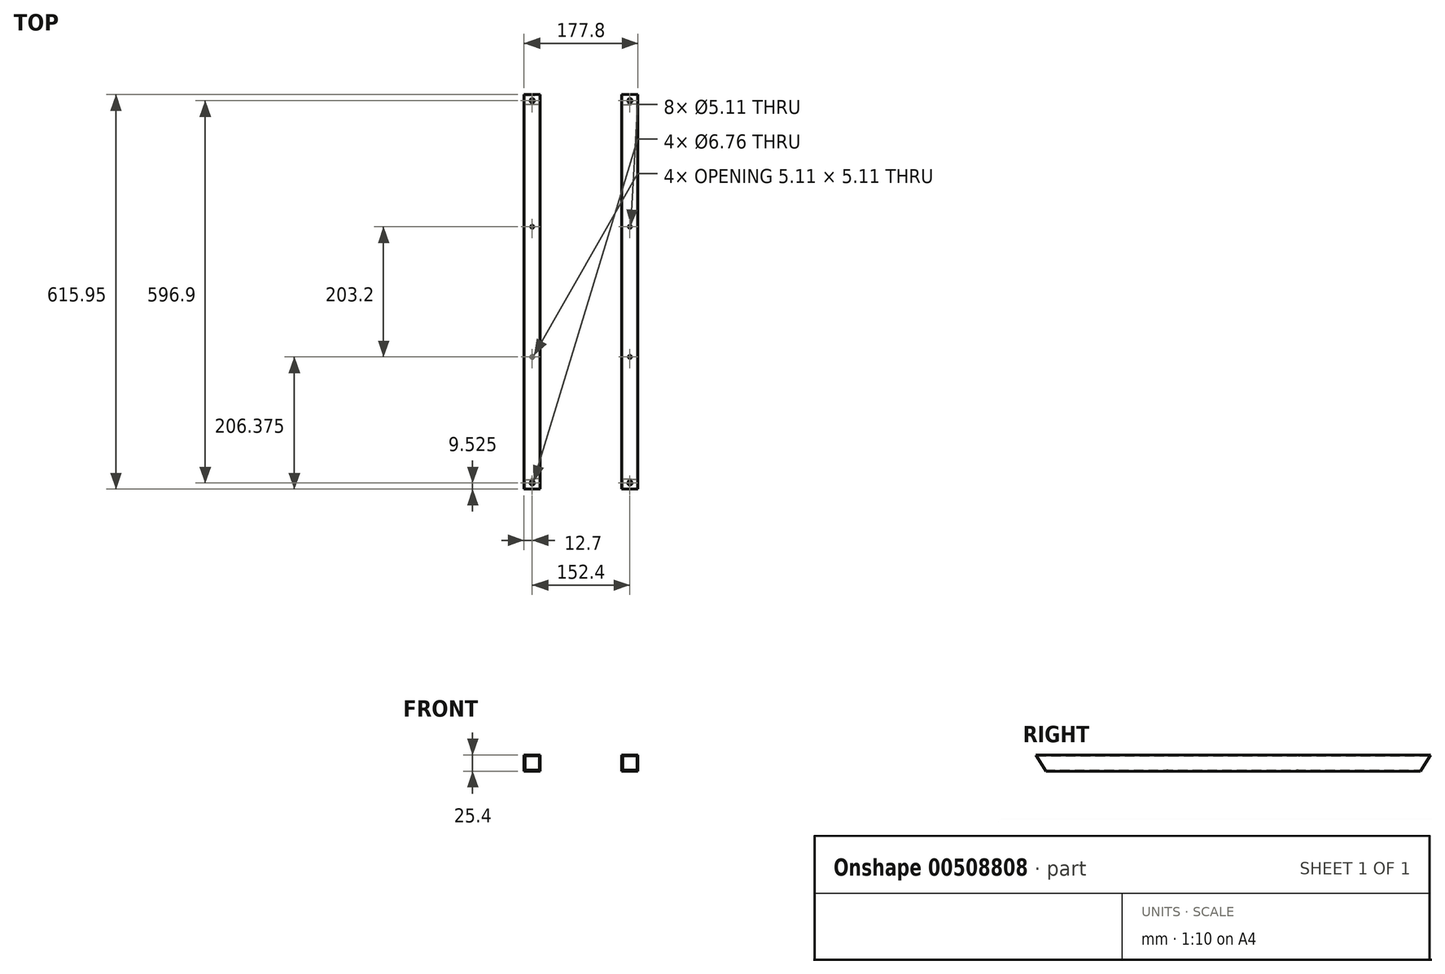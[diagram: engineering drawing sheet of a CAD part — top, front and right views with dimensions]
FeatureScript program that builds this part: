
annotation { "Feature Type Name" : "Feature", "Feature Type Description" : "" }
export const myFeature = defineFeature(function(context is Context, id is Id, definition is map)
    precondition{}
    {
        {
            var Q0;
            Q0=qCreatedBy(makeId("Front.planeOp"),FACE);
            var sketch = newSketch(context, id + "F0", { "sketchPlane" : qUnion([Q0])});
            skLineSegment(sketch, "E0.bottom", {"start": v(63.5, 25.4) * mm, "end": v(88.9, 25.4) * mm});
            skLineSegment(sketch, "E0.top", {"start": v(63.5, 0) * mm, "end": v(88.9, 0) * mm});
            skLineSegment(sketch, "E0.left", {"start": v(63.5, 25.4) * mm, "end": v(63.5, 0) * mm});
            skLineSegment(sketch, "E0.right", {"start": v(88.9, 25.4) * mm, "end": v(88.9, 0) * mm});
            skLineSegment(sketch, "E1.bottom", {"start": v(87.31, 1.59) * mm, "end": v(65.09, 1.59) * mm});
            skLineSegment(sketch, "E1.top", {"start": v(87.31, 23.81) * mm, "end": v(65.09, 23.81) * mm});
            skLineSegment(sketch, "E1.left", {"start": v(87.31, 1.59) * mm, "end": v(87.31, 23.81) * mm});
            skLineSegment(sketch, "E1.right", {"start": v(65.09, 1.59) * mm, "end": v(65.09, 23.81) * mm});
            skSolve(sketch);
        }
        {
            var Q0;
            Q0 = qSketchRegion(id + "F0", true);
            extrude(context, id + "F1", {"entities" : qUnion([Q0]), "depth" : 615.95 * mm, "offsetDistance" : 25.4 * mm});
        }
        {
            var Q0;
            Q0=makeQuery(id+"F1.opExtrude","SWEPT_FACE",FACE,{"disambiguationData":[OSD([sQuery(id+"F0.wireOp",EDGE,"E0.bottom")])]});
            var sketch = newSketch(context, id + "F2", { "sketchPlane" : qUnion([Q0])});
            skLineSegment(sketch, "E2", {"start": v(63.5, -307.98) * mm, "end": v(88.9, -307.98) * mm, "construction": true});
            skPoint(sketch, "E3", {"position": v(76.2, -409.58) * mm});
            skPoint(sketch, "E4.MirrorP", {"position": v(76.2, -206.38) * mm});
            skSolve(sketch);
        }
        {
            var Q0;
            Q0=sQuery(id+"F2.wireOp",VERTEX,"E4.MirrorP");
            var Q1;
            Q1=sQuery(id+"F2.wireOp",VERTEX,"E3");
            var Q2;
            Q2=makeQuery(id+"F1.opExtrude","SWEPT_BODY",BODY,{"disambiguationData":[OSD([sQuery(id+"F0.wireOp",EDGE,"E0.bottom"),sQuery(id+"F0.wireOp",EDGE,"E0.top"),sQuery(id+"F0.wireOp",EDGE,"E0.left"),sQuery(id+"F0.wireOp",EDGE,"E0.right"),sQuery(id+"F0.wireOp",EDGE,"E1.bottom"),sQuery(id+"F0.wireOp",EDGE,"E1.top"),sQuery(id+"F0.wireOp",EDGE,"E1.left"),sQuery(id+"F0.wireOp",EDGE,"E1.right")])]});
            hole(context, id + "F3", {"style" : HoleStyle.SIMPLE, "endStyle" : HoleEndStyle.THROUGH, "standardTappedOrClearance" : lookupTablePath({ "standard" : "ANSI", "fit" : "Normal (ASME)", "size" : "#10", "type" : "Clearance" }), "standardBlindInLast" : lookupTablePath({ "fit" : "Free", "standard" : "ANSI", "size" : "#10", "type" : "Clearance" }), "holeDiameter" : 5.1 * mm, "isTappedThrough" : true, "tappedDepth" : 12.7 * mm, "tapClearance" : 3, "locations" : qUnion([Q0, Q1]), "scope" : qUnion([Q2])});
        }
        {
            var Q0;
            Q0=makeQuery(id+"F1.opExtrude","SWEPT_FACE",FACE,{"disambiguationData":[OSD([sQuery(id+"F0.wireOp",EDGE,"E0.right")])]});
            var sketch = newSketch(context, id + "F4", { "sketchPlane" : qUnion([Q0])});
            skLineSegment(sketch, "E5", {"start": v(0, 25.4) * mm, "end": v(-15.88, 0) * mm});
            skLineSegment(sketch, "E6", {"start": v(-15.88, 0) * mm, "end": v(0, 0) * mm});
            skLineSegment(sketch, "E7", {"start": v(0, 0) * mm, "end": v(0, 25.4) * mm});
            skLineSegment(sketch, "E8", {"start": v(-307.98, 25.4) * mm, "end": v(-307.98, 0) * mm, "construction": true});
            skLineSegment(sketch, "E9.MirrorCS", {"start": v(-600.08, 0) * mm, "end": v(-615.95, 0) * mm});
            skLineSegment(sketch, "E10.MirrorCS", {"start": v(-615.95, 0) * mm, "end": v(-615.95, 25.4) * mm});
            skLineSegment(sketch, "E11.MirrorCS", {"start": v(-615.95, 25.4) * mm, "end": v(-600.08, 0) * mm});
            skSolve(sketch);
        }
        {
            var Q0;
            {var subQ0=sQuery(id+"F4.wireOp",EDGE,"WcfWc3fK-U80W-BFk6-5zm0-iw6WaQoH4Mpi");Q0=makeQuery(id+"F4.imprint","IMPRINT",FACE,{"disambiguationData":[TD([[makeQuery(id+"F4.imprint","IMPRINT",EDGE,{"derivedFrom":subQ0}),-1.0]])]});}
            var Q1;
            Q1=makeQuery(id+"F4.imprint","IMPRINT",FACE,{"disambiguationData":[TD([[makeQuery(id+"F4.imprint","IMPRINT",EDGE,{"derivedFrom":sQuery(id+"F4.wireOp",EDGE,"E5")}),1.0]])]});
            var Q2;
            Q2=makeQuery(id+"F4.imprint","IMPRINT",FACE,{"disambiguationData":[TD([[makeQuery(id+"F4.imprint","IMPRINT",EDGE,{"derivedFrom":sQuery(id+"F4.wireOp",EDGE,"E9.MirrorCS")}),1.0]])]});
            extrude(context, id + "F5", {"entities" : qUnion([Q0, Q1, Q2]), "operationType" : NewBodyOperationType.REMOVE, "oppositeDirection" : true, "depth" : 25.4 * mm, "offsetDistance" : 25.4 * mm});
        }
        {
            var Q0;
            Q0=makeQuery(id+"F1.opExtrude","SWEPT_FACE",FACE,{"disambiguationData":[OSD([sQuery(id+"F0.wireOp",EDGE,"E0.top")])]});
            var sketch = newSketch(context, id + "F6", { "sketchPlane" : qUnion([Q0])});
            skPoint(sketch, "E12", {"position": v(76.2, 206.38) * mm});
            skPoint(sketch, "E13", {"position": v(76.2, 409.58) * mm});
            skSolve(sketch);
        }
        {
            var Q0;
            Q0=sQuery(id+"F6.wireOp",VERTEX,"E13");
            var Q1;
            Q1=sQuery(id+"F6.wireOp",VERTEX,"E12");
            var Q2;
            Q2=makeQuery(id+"F1.opExtrude","SWEPT_BODY",BODY,{"disambiguationData":[OSD([sQuery(id+"F0.wireOp",EDGE,"E0.bottom"),sQuery(id+"F0.wireOp",EDGE,"E0.top"),sQuery(id+"F0.wireOp",EDGE,"E0.left"),sQuery(id+"F0.wireOp",EDGE,"E0.right"),sQuery(id+"F0.wireOp",EDGE,"E1.bottom"),sQuery(id+"F0.wireOp",EDGE,"E1.top"),sQuery(id+"F0.wireOp",EDGE,"E1.left"),sQuery(id+"F0.wireOp",EDGE,"E1.right")])]});
            hole(context, id + "F7", {"style" : HoleStyle.SIMPLE, "endStyle" : HoleEndStyle.BLIND, "standardTappedOrClearance" : lookupTablePath({ "standard" : "ANSI", "size" : "1/2 (0.5)", "type" : "Drilled" }), "standardBlindInLast" : lookupTablePath({ "standard" : "ANSI", "size" : "1/2", "type" : "Drilled" }), "holeDiameter" : 1 / 50.8 * mm, "holeDepth" : 1.59 * mm, "isTappedThrough" : true, "tappedDepth" : 12.7 * mm, "tapClearance" : 3, "locations" : qUnion([Q0, Q1]), "scope" : qUnion([Q2])});
        }
        {
            var Q0;
            {var subQ0=sQuery(id+"F0.wireOp",EDGE,"E0.bottom");Q0=makeQuery(id+"F2.imprint","IMPRINT",FACE,{"disambiguationData":[TD([[makeQuery(id+"F2.imprint","IMPRINT",EDGE,{"derivedFrom":makeQuery(id+"F1.opExtrude","CAP_EDGE",EDGE,{"disambiguationData":[OSD([subQ0])],"isStart":true})}),-1.0]])]});}
            var sketch = newSketch(context, id + "F8", { "sketchPlane" : qUnion([Q0])});
            skPoint(sketch, "E14", {"position": v(76.2, -9.53) * mm});
            skPoint(sketch, "E15.MirrorP", {"position": v(76.2, -606.43) * mm});
            skSolve(sketch);
        }
        {
            var Q0;
            Q0=sQuery(id+"F8.wireOp",VERTEX,"E15.MirrorP");
            var Q1;
            Q1=sQuery(id+"F8.wireOp",VERTEX,"E14");
            var Q2;
            Q2=makeQuery(id+"F1.opExtrude","SWEPT_BODY",BODY,{"disambiguationData":[OSD([sQuery(id+"F0.wireOp",EDGE,"E0.bottom"),sQuery(id+"F0.wireOp",EDGE,"E0.top"),sQuery(id+"F0.wireOp",EDGE,"E0.left"),sQuery(id+"F0.wireOp",EDGE,"E0.right"),sQuery(id+"F0.wireOp",EDGE,"E1.bottom"),sQuery(id+"F0.wireOp",EDGE,"E1.top"),sQuery(id+"F0.wireOp",EDGE,"E1.left"),sQuery(id+"F0.wireOp",EDGE,"E1.right")])]});
            hole(context, id + "F9", {"style" : HoleStyle.SIMPLE, "endStyle" : HoleEndStyle.THROUGH, "standardTappedOrClearance" : lookupTablePath({ "standard" : "ANSI", "fit" : "Normal (ASME)", "size" : "1/4", "type" : "Clearance" }), "standardBlindInLast" : lookupTablePath({ "fit" : "Free", "standard" : "ANSI", "size" : "1/4", "type" : "Clearance" }), "holeDiameter" : 6.76 * mm, "isTappedThrough" : true, "tappedDepth" : 12.7 * mm, "tapClearance" : 3, "locations" : qUnion([Q0, Q1]), "scope" : qUnion([Q2])});
        }
        {
            var Q0;
            Q0=makeQuery(id+"F1.opExtrude","SWEPT_BODY",BODY,{"disambiguationData":[OSD([sQuery(id+"F0.wireOp",EDGE,"E0.bottom"),sQuery(id+"F0.wireOp",EDGE,"E0.top"),sQuery(id+"F0.wireOp",EDGE,"E0.left"),sQuery(id+"F0.wireOp",EDGE,"E0.right"),sQuery(id+"F0.wireOp",EDGE,"E1.bottom"),sQuery(id+"F0.wireOp",EDGE,"E1.top"),sQuery(id+"F0.wireOp",EDGE,"E1.left"),sQuery(id+"F0.wireOp",EDGE,"E1.right")])]});
            var Q1;
            Q1=qCreatedBy(makeId("Right.planeOp"),FACE);
            mirror(context, id + "F10", {"entities" : qUnion([Q0]), "mirrorPlane" : qUnion([Q1])});
        }
    });
